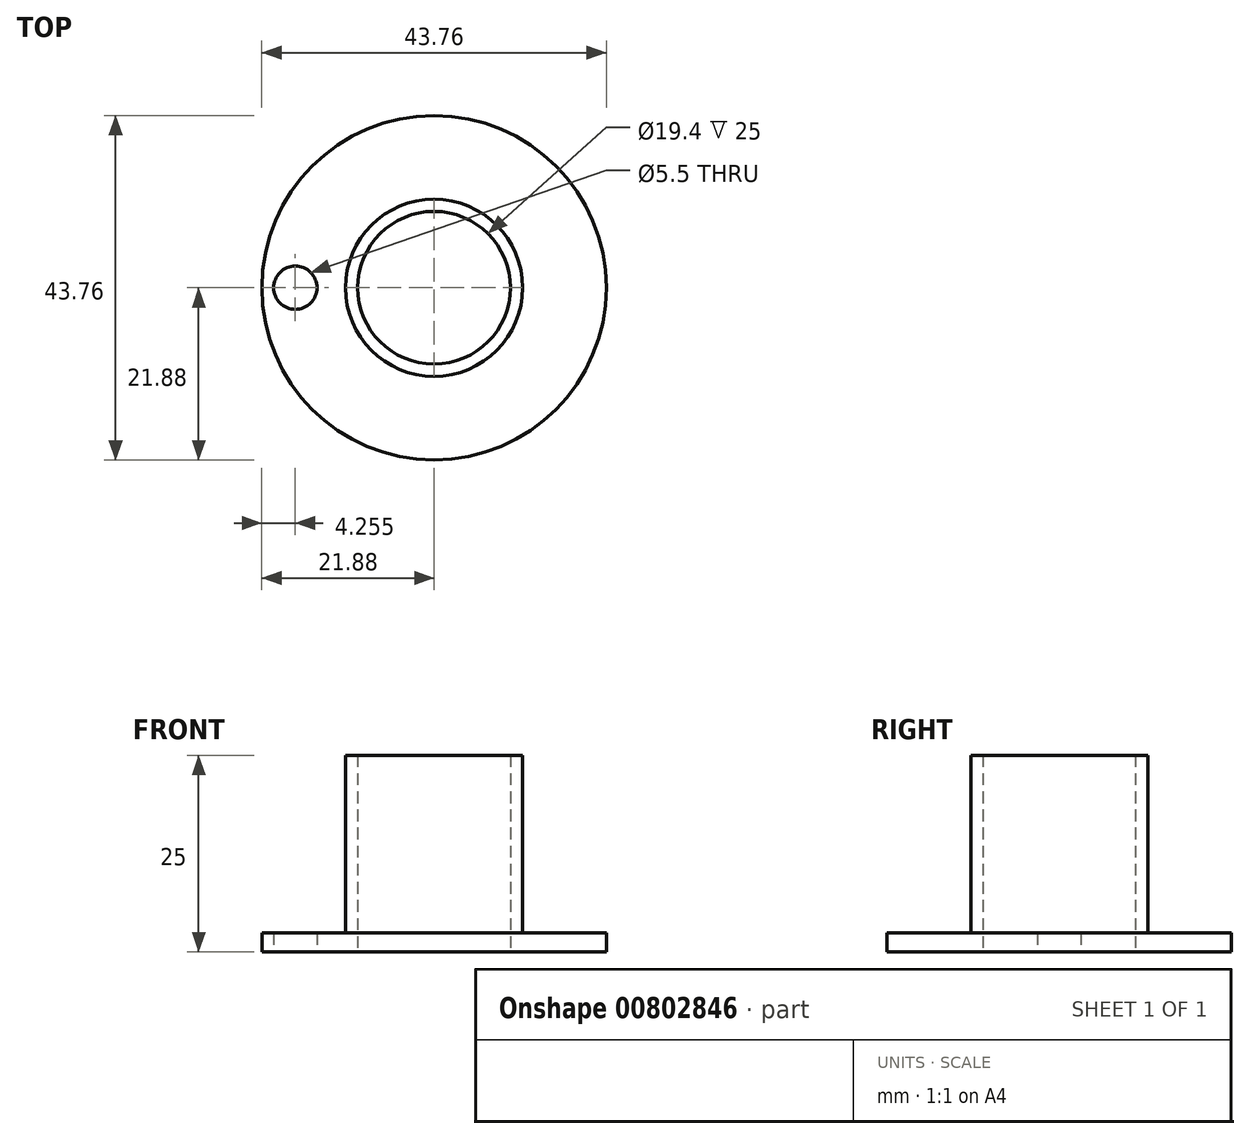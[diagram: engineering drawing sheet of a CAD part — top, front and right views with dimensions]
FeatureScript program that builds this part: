
annotation { "Feature Type Name" : "Feature", "Feature Type Description" : "" }
export const myFeature = defineFeature(function(context is Context, id is Id, definition is map)
    precondition{}
    {
        {
            var Q0;
            Q0=qCreatedBy(makeId("Top.planeOp"),FACE);
            var sketch = newSketch(context, id + "F0", { "sketchPlane" : qUnion([Q0])});
            skCircle(sketch, "E0", {"center": v(0, 0) * mm, "radius": 21.88 * mm});
            skCircle(sketch, "E1", {"center": v(0, 0) * mm, "radius": 11.25 * mm});
            skCircle(sketch, "E2", {"center": v(0, 0) * mm, "radius": 9.7 * mm});
            skCircle(sketch, "E3", {"center": v(0, 0) * mm, "radius": 17.62 * mm, "construction": true});
            skPoint(sketch, "E4", {"position": v(-17.62, 0) * mm});
            skSolve(sketch);
        }
        {
            var Q0;
            Q0=makeQuery(id+"F0.imprint","IMPRINT",FACE,{"disambiguationData":[TD([[makeQuery(id+"F0.imprint","IMPRINT",EDGE,{"derivedFrom":sQuery(id+"F0.wireOp",EDGE,"E0")}),1.0]])]});
            var Q1;
            Q1=makeQuery(id+"F0.imprint","IMPRINT",FACE,{"disambiguationData":[TD([[makeQuery(id+"F0.imprint","IMPRINT",EDGE,{"derivedFrom":sQuery(id+"F0.wireOp",EDGE,"E1")}),1.0]])]});
            extrude(context, id + "F1", {"entities" : qUnion([Q0, Q1]), "depth" : 2.4 * mm, "offsetDistance" : 25 * mm});
        }
        {
            var Q0;
            Q0=makeQuery(id+"F0.imprint","IMPRINT",FACE,{"disambiguationData":[TD([[makeQuery(id+"F0.imprint","IMPRINT",EDGE,{"derivedFrom":sQuery(id+"F0.wireOp",EDGE,"E1")}),1.0]])]});
            extrude(context, id + "F2", {"entities" : qUnion([Q0]), "operationType" : NewBodyOperationType.ADD, "depth" : 25 * mm, "offsetDistance" : 25 * mm});
        }
        {
            var Q0;
            Q0=sQuery(id+"F0.wireOp",VERTEX,"E4");
            var Q1;
            Q1=makeQuery(id+"F1.opExtrude","SWEPT_BODY",BODY,{"disambiguationData":[OSD([sQuery(id+"F0.wireOp",EDGE,"E0"),sQuery(id+"F0.wireOp",EDGE,"E2")])]});
            hole(context, id + "F3", {"style" : HoleStyle.SIMPLE, "endStyle" : HoleEndStyle.THROUGH, "oppositeDirection" : true, "standardTappedOrClearance" : lookupTablePath({ "standard" : "ISO", "fit" : "Normal", "size" : "M5", "type" : "Clearance" }), "standardBlindInLast" : lookupTablePath({ "fit" : "Standard", "standard" : "ISO", "size" : "M5", "type" : "Clearance" }), "holeDiameter" : 5.5 * mm, "majorDiameter" : 5 * mm, "tappedDepth" : 12 * mm, "tapClearance" : 3, "locations" : qUnion([Q0]), "scope" : qUnion([Q1])});
        }
        {
            var Q0;
            Q0=qCreatedBy(makeId("Front.planeOp"),FACE);
            var sketch = newSketch(context, id + "F4", { "sketchPlane" : qUnion([Q0])});
            skLineSegment(sketch, "E5", {"start": v(0, 57.28) * mm, "end": v(0, -41.7) * mm, "construction": true});
            skSolve(sketch);
        }
    });
